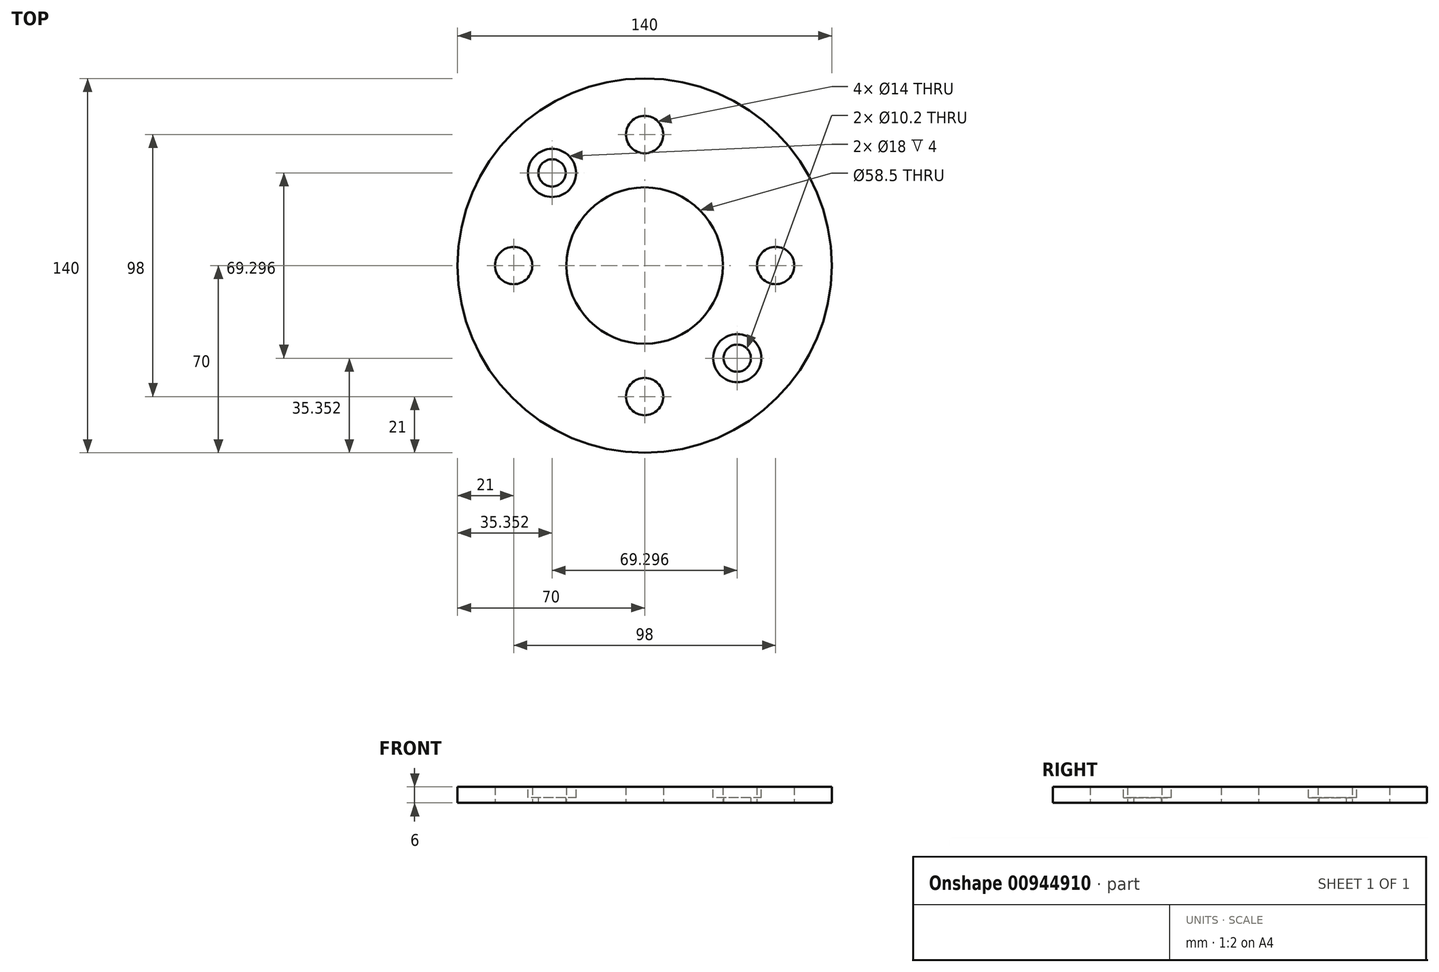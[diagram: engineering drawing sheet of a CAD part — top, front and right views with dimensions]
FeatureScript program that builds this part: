
annotation { "Feature Type Name" : "Feature", "Feature Type Description" : "" }
export const myFeature = defineFeature(function(context is Context, id is Id, definition is map)
    precondition{}
    {
        {
            var Q0;
            Q0=qCreatedBy(makeId("Top.planeOp"),FACE);
            var sketch = newSketch(context, id + "F0", { "sketchPlane" : qUnion([Q0])});
            skCircle(sketch, "E0", {"center": v(0, 0) * mm, "radius": 29.25 * mm});
            skCircle(sketch, "E1", {"center": v(0, 0) * mm, "radius": 49 * mm, "construction": true});
            skCircle(sketch, "E2", {"center": v(0, 0) * mm, "radius": 70 * mm});
            skCircle(sketch, "E3", {"center": v(0, 49) * mm, "radius": 7 * mm});
            skCircle(sketch, "E4.1.0", {"center": v(-49, 0) * mm, "radius": 7 * mm});
            skCircle(sketch, "E4.2.0", {"center": v(0, -49) * mm, "radius": 7 * mm});
            skCircle(sketch, "E4.3.0", {"center": v(49, 0) * mm, "radius": 7 * mm});
            skLineSegment(sketch, "E5", {"start": v(34.65, -34.65) * mm, "end": v(0, 0) * mm, "construction": true});
            skCircle(sketch, "E6", {"center": v(-34.65, 34.65) * mm, "radius": 5.1 * mm});
            skCircle(sketch, "E7", {"center": v(34.65, -34.65) * mm, "radius": 5.1 * mm});
            skSolve(sketch);
        }
        {
            var Q0;
            Q0=makeQuery(id+"F0.imprint","IMPRINT",FACE,{"disambiguationData":[TD([[makeQuery(id+"F0.imprint","IMPRINT",EDGE,{"derivedFrom":sQuery(id+"F0.wireOp",EDGE,"E0")}),-1.0]])]});
            extrude(context, id + "F1", {"entities" : qUnion([Q0]), "depth" : 6 * mm, "offsetDistance" : 25 * mm});
        }
        {
            var Q0;
            Q0=makeQuery(id+"F1.opExtrude","CAP_FACE",FACE,{"disambiguationData":[OSD([sQuery(id+"F0.wireOp",EDGE,"E0"),sQuery(id+"F0.wireOp",EDGE,"E2"),sQuery(id+"F0.wireOp",EDGE,"E3"),sQuery(id+"F0.wireOp",EDGE,"E4.1.0"),sQuery(id+"F0.wireOp",EDGE,"E4.2.0"),sQuery(id+"F0.wireOp",EDGE,"E4.3.0"),sQuery(id+"F0.wireOp",EDGE,"E6"),sQuery(id+"F0.wireOp",EDGE,"E7")])],"isStart":false});
            var sketch = newSketch(context, id + "F2", { "sketchPlane" : qUnion([Q0])});
            skCircle(sketch, "E8", {"center": v(-34.65, 34.65) * mm, "radius": 9 * mm});
            skCircle(sketch, "E9", {"center": v(34.65, -34.65) * mm, "radius": 9 * mm});
            skSolve(sketch);
        }
        {
            var Q0;
            Q0=makeQuery(id+"F2.imprint","IMPRINT",FACE,{"disambiguationData":[TD([[makeQuery(id+"F2.imprint","IMPRINT",EDGE,{"derivedFrom":sQuery(id+"F2.wireOp",EDGE,"E8")}),1.0]])]});
            var Q1;
            Q1=makeQuery(id+"F2.imprint","IMPRINT",FACE,{"disambiguationData":[TD([[makeQuery(id+"F2.imprint","IMPRINT",EDGE,{"derivedFrom":sQuery(id+"F2.wireOp",EDGE,"E9")}),1.0]])]});
            extrude(context, id + "F3", {"entities" : qUnion([Q0, Q1]), "operationType" : NewBodyOperationType.REMOVE, "oppositeDirection" : true, "depth" : 4 * mm, "offsetDistance" : 25 * mm});
        }
    });
